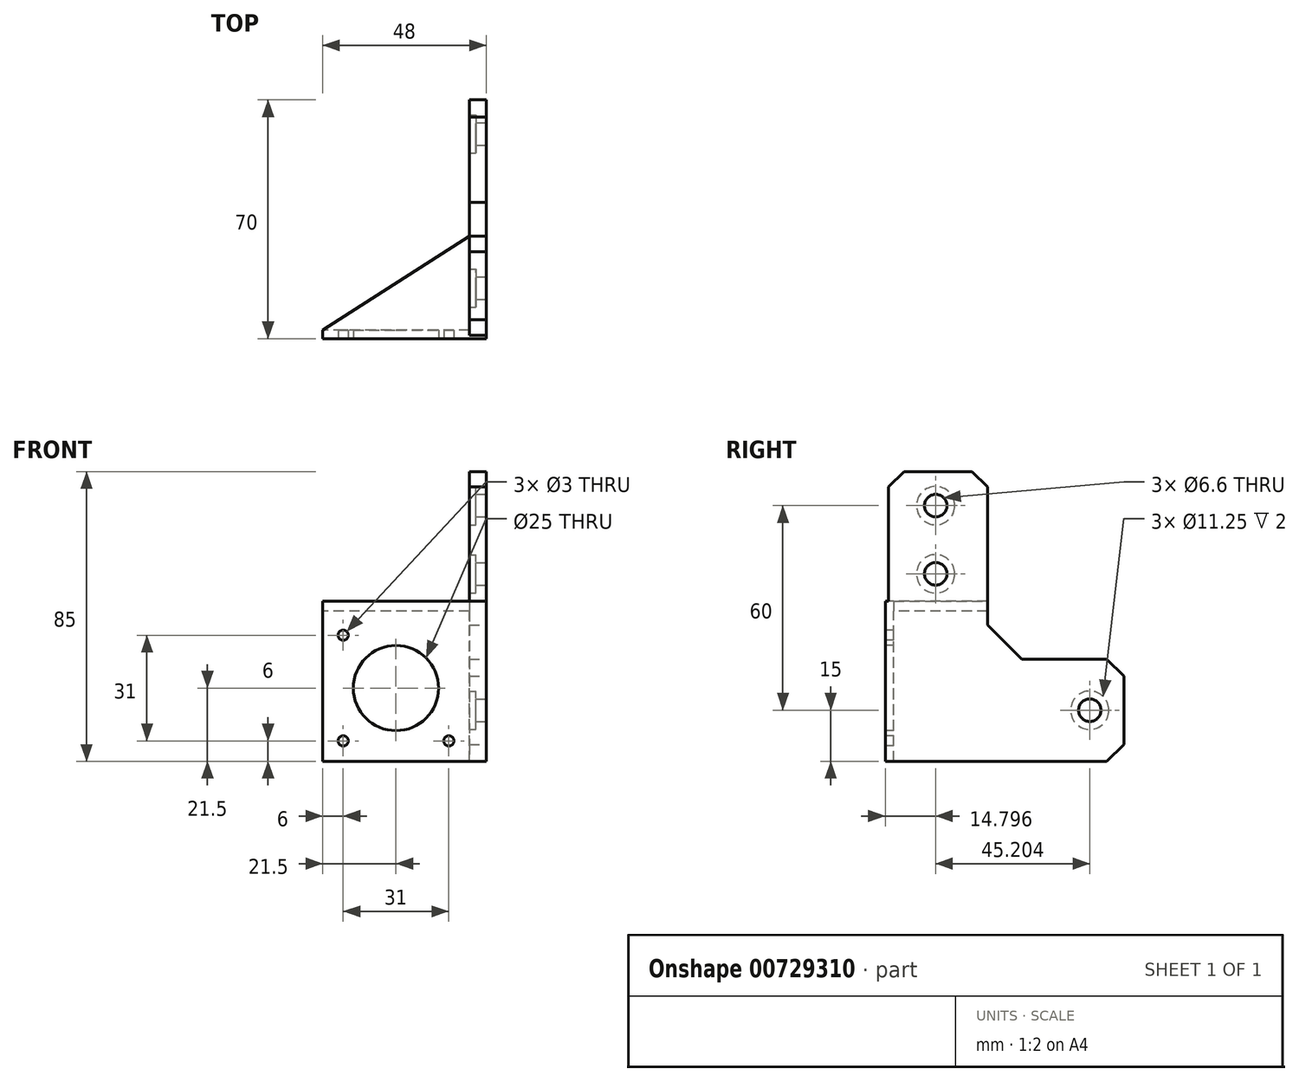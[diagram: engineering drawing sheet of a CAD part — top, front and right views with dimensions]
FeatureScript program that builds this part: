
annotation { "Feature Type Name" : "Feature", "Feature Type Description" : "" }
export const myFeature = defineFeature(function(context is Context, id is Id, definition is map)
    precondition{}
    {
        {
            var Q0;
            Q0=qCreatedBy(makeId("Front.planeOp"),FACE);
            var sketch = newSketch(context, id + "F0", { "sketchPlane" : qUnion([Q0])});
            skLineSegment(sketch, "E0.bottom", {"start": v(0, 0) * mm, "end": v(-48, 0) * mm});
            skLineSegment(sketch, "E0.top", {"start": v(0, 43) * mm, "end": v(-48, 43) * mm});
            skLineSegment(sketch, "E0.left", {"start": v(0, 0) * mm, "end": v(0, 43) * mm});
            skLineSegment(sketch, "E0.right", {"start": v(-48, 0) * mm, "end": v(-48, 43) * mm});
            skLineSegment(sketch, "E1.bottom", {"start": v(-42, 37) * mm, "end": v(-11, 37) * mm, "construction": true});
            skLineSegment(sketch, "E1.top", {"start": v(-42, 6) * mm, "end": v(-11, 6) * mm, "construction": true});
            skLineSegment(sketch, "E1.left", {"start": v(-42, 37) * mm, "end": v(-42, 6) * mm, "construction": true});
            skLineSegment(sketch, "E1.right", {"start": v(-11, 37) * mm, "end": v(-11, 6) * mm, "construction": true});
            skPoint(sketch, "E1.middle", {"position": v(-26.5, 21.5) * mm});
            skLineSegment(sketch, "E2", {"start": v(-48, 43) * mm, "end": v(-5, 0) * mm, "construction": true});
            skPoint(sketch, "E3", {"position": v(-48, 21.5) * mm});
            skCircle(sketch, "E4", {"center": v(-42, 37) * mm, "radius": 1.5 * mm});
            skCircle(sketch, "E5", {"center": v(-42, 6) * mm, "radius": 1.5 * mm});
            skCircle(sketch, "E6", {"center": v(-11, 6) * mm, "radius": 1.5 * mm});
            skCircle(sketch, "E7", {"center": v(-26.5, 21.5) * mm, "radius": 12.5 * mm});
            skSolve(sketch);
        }
        {
            var Q0;
            Q0=makeQuery(id+"F0.imprint","IMPRINT",FACE,{"disambiguationData":[TD([[makeQuery(id+"F0.imprint","IMPRINT",EDGE,{"derivedFrom":sQuery(id+"F0.wireOp",EDGE,"E0.bottom")}),-1.0]])]});
            extrude(context, id + "F1", {"entities" : qUnion([Q0]), "oppositeDirection" : true, "depth" : 2.5 * mm, "offsetDistance" : 25 * mm});
        }
        {
            var Q0;
            Q0=qCreatedBy(makeId("Right.planeOp"),FACE);
            var sketch = newSketch(context, id + "F2", { "sketchPlane" : qUnion([Q0])});
            skLineSegment(sketch, "E8", {"start": v(0, 43) * mm, "end": v(1, 43) * mm});
            skLineSegment(sketch, "E9", {"start": v(1, 43) * mm, "end": v(1, 80.5) * mm});
            skLineSegment(sketch, "E10", {"start": v(1, 80.5) * mm, "end": v(5.5, 85) * mm});
            skLineSegment(sketch, "E11", {"start": v(5.5, 85) * mm, "end": v(25.5, 85) * mm});
            skLineSegment(sketch, "E12", {"start": v(25.5, 85) * mm, "end": v(30, 80.5) * mm});
            skLineSegment(sketch, "E13", {"start": v(30, 80.5) * mm, "end": v(30, 40) * mm});
            skLineSegment(sketch, "E14", {"start": v(30, 40) * mm, "end": v(40, 30) * mm});
            skLineSegment(sketch, "E15", {"start": v(40, 30) * mm, "end": v(65, 30) * mm});
            skLineSegment(sketch, "E16", {"start": v(65, 30) * mm, "end": v(70, 25) * mm});
            skLineSegment(sketch, "E17", {"start": v(70, 25) * mm, "end": v(70, 5) * mm});
            skLineSegment(sketch, "E18", {"start": v(70, 5) * mm, "end": v(65, 0) * mm});
            skLineSegment(sketch, "E19", {"start": v(65, 0) * mm, "end": v(0, 0) * mm});
            skLineSegment(sketch, "E20", {"start": v(0, 0) * mm, "end": v(0, 43) * mm});
            skSolve(sketch);
        }
        {
            var Q0;
            Q0=makeQuery(id+"F2.imprint","IMPRINT",FACE,{"disambiguationData":[TD([[makeQuery(id+"F2.imprint","IMPRINT",EDGE,{"derivedFrom":sQuery(id+"F2.wireOp",EDGE,"E8")}),-1.0]])]});
            extrude(context, id + "F3", {"entities" : qUnion([Q0]), "operationType" : NewBodyOperationType.ADD, "oppositeDirection" : true, "depth" : 5 * mm, "offsetDistance" : 25 * mm});
        }
        {
            var Q0;
            Q0=makeQuery(id+"F3.opExtrude","CAP_FACE",FACE,{"disambiguationData":[OSD([sQuery(id+"F2.wireOp",EDGE,"E8"),sQuery(id+"F2.wireOp",EDGE,"E9"),sQuery(id+"F2.wireOp",EDGE,"E10"),sQuery(id+"F2.wireOp",EDGE,"E11"),sQuery(id+"F2.wireOp",EDGE,"E12"),sQuery(id+"F2.wireOp",EDGE,"E13"),sQuery(id+"F2.wireOp",EDGE,"E14"),sQuery(id+"F2.wireOp",EDGE,"E15"),sQuery(id+"F2.wireOp",EDGE,"E16"),sQuery(id+"F2.wireOp",EDGE,"E17"),sQuery(id+"F2.wireOp",EDGE,"E18"),sQuery(id+"F2.wireOp",EDGE,"E19"),sQuery(id+"F2.wireOp",EDGE,"E20")])],"isStart":false});
            var sketch = newSketch(context, id + "F4", { "sketchPlane" : qUnion([Q0])});
            skPoint(sketch, "E21", {"position": v(-14.8, 75) * mm});
            skPoint(sketch, "E22", {"position": v(-14.8, 55) * mm});
            skPoint(sketch, "E23", {"position": v(-60, 15) * mm});
            skPoint(sketch, "E23.positionSnap0", {"position": v(-70, 15) * mm});
            skSolve(sketch);
        }
        {
            var Q0;
            Q0=sQuery(id+"F4.wireOp",VERTEX,"E21");
            var Q1;
            Q1=sQuery(id+"F4.wireOp",VERTEX,"E22");
            var Q2;
            Q2=sQuery(id+"F4.wireOp",VERTEX,"E23");
            var Q3;
            Q3=makeQuery(id+"F1.opExtrude","SWEPT_BODY",BODY,{"disambiguationData":[OSD([sQuery(id+"F0.wireOp",EDGE,"E0.bottom"),sQuery(id+"F0.wireOp",EDGE,"E0.top"),sQuery(id+"F0.wireOp",EDGE,"E0.left"),sQuery(id+"F0.wireOp",EDGE,"E0.right"),sQuery(id+"F0.wireOp",EDGE,"E4"),sQuery(id+"F0.wireOp",EDGE,"E5"),sQuery(id+"F0.wireOp",EDGE,"E6"),sQuery(id+"F0.wireOp",EDGE,"E7")])]});
            hole(context, id + "F5", {"style" : HoleStyle.C_BORE, "endStyle" : HoleEndStyle.BLIND, "holeDiameter" : 6.6 * mm, "cBoreDiameter" : 11.25 * mm, "cBoreDepth" : 2 * mm, "majorDiameter" : 5 * mm, "holeDepth" : 20 * mm, "isTappedThrough" : true, "tappedDepth" : 12 * mm, "tapClearance" : 3, "locations" : qUnion([Q0, Q1, Q2]), "scope" : qUnion([Q3])});
        }
        {
            var Q0;
            Q0=makeQuery(id+"F1.opExtrude","SWEPT_FACE",FACE,{"disambiguationData":[OSD([sQuery(id+"F0.wireOp",EDGE,"E0.top")])]});
            var sketch = newSketch(context, id + "F6", { "sketchPlane" : qUnion([Q0])});
            skLineSegment(sketch, "E24", {"start": v(-48, 0) * mm, "end": v(-48, 2.5) * mm});
            skLineSegment(sketch, "E25", {"start": v(-48, 2.5) * mm, "end": v(-5, 30) * mm});
            skLineSegment(sketch, "E26", {"start": v(-5, 30) * mm, "end": v(0, 30) * mm});
            skLineSegment(sketch, "E27", {"start": v(0, 30) * mm, "end": v(0, 0) * mm});
            skLineSegment(sketch, "E28", {"start": v(0, 0) * mm, "end": v(-48, 0) * mm});
            skSolve(sketch);
        }
        {
            var Q0;
            Q0=makeQuery(id+"F6.imprint","IMPRINT",FACE,{"disambiguationData":[TD([[makeQuery(id+"F6.imprint","IMPRINT",EDGE,{"derivedFrom":sQuery(id+"F6.wireOp",EDGE,"E25")}),-1.0]])]});
            var Q1;
            Q1=makeQuery(id+"F6.imprint","IMPRINT",FACE,{"disambiguationData":[TD([[makeQuery(id+"F6.imprint","IMPRINT",EDGE,{"derivedFrom":sQuery(id+"F6.wireOp",EDGE,"E24")}),1.0]])]});
            extrude(context, id + "F7", {"entities" : qUnion([Q0, Q1]), "operationType" : NewBodyOperationType.ADD, "depth" : 4 * mm, "offsetDistance" : 25 * mm});
        }
        {
            var Q0;
            Q0=makeQuery(id+"F7.opExtrude","CAP_FACE",FACE,{"disambiguationData":[OSD([sQuery(id+"F6.wireOp",EDGE,"E24"),sQuery(id+"F6.wireOp",EDGE,"E25"),sQuery(id+"F6.wireOp",EDGE,"E26"),sQuery(id+"F6.wireOp",EDGE,"E27"),sQuery(id+"F6.wireOp",EDGE,"E28")])],"isStart":true});
            extrude(context, id + "F8", {"entities" : qUnion([Q0]), "operationType" : NewBodyOperationType.REMOVE, "oppositeDirection" : true, "depth" : 1 * mm, "offsetDistance" : 25 * mm});
        }
    });
